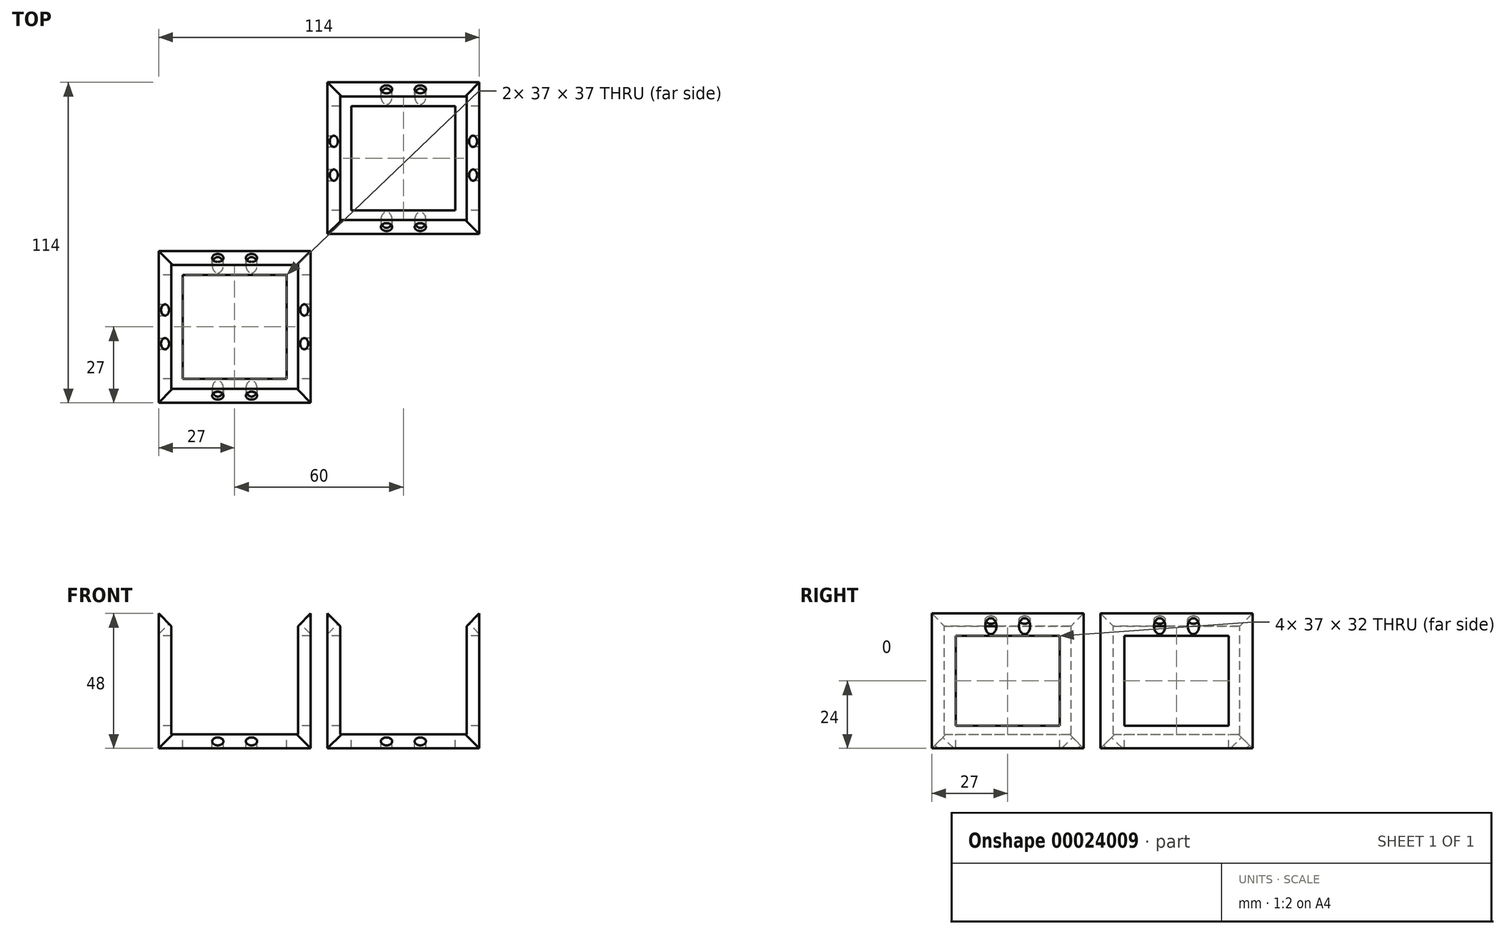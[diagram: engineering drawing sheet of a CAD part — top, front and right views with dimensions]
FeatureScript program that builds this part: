
annotation { "Feature Type Name" : "Feature", "Feature Type Description" : "" }
export const myFeature = defineFeature(function(context is Context, id is Id, definition is map)
    precondition{}
    {
        {
            var Q0;
            Q0=qCreatedBy(makeId("Top.planeOp"),FACE);
            var sketch = newSketch(context, id + "F0", { "sketchPlane" : qUnion([Q0])});
            skPoint(sketch, "E0.rect.middle", {"position": v(0, 0) * mm});
            skLineSegment(sketch, "E1.rect.bottom", {"start": v(27, 27) * mm, "end": v(-27, 27) * mm});
            skLineSegment(sketch, "E2", {"start": v(27, 27) * mm, "end": v(27, -27) * mm});
            skLineSegment(sketch, "E3", {"start": v(-27, -27) * mm, "end": v(0, -27) * mm});
            skLineSegment(sketch, "E4", {"start": v(0, -27) * mm, "end": v(27, -27) * mm});
            skLineSegment(sketch, "E5", {"start": v(-27, 27) * mm, "end": v(-27, 0) * mm});
            skLineSegment(sketch, "E6", {"start": v(-27, 0) * mm, "end": v(-27, -27) * mm});
            skSolve(sketch);
        }
        {
            var Q0;
            Q0 = qSketchRegion(id + "F0", true);
            extrude(context, id + "F1", {"entities" : qUnion([Q0]), "depth" : 48 * mm});
        }
        {
            var Q0;
            Q0=makeQuery(id+"F1.opExtrude","SWEPT_FACE",FACE,{"disambiguationData":[OSD([sQuery(id+"F0.wireOp",EDGE,"E3"),sQuery(id+"F0.wireOp",EDGE,"E4")])]});
            var sketch = newSketch(context, id + "F2", { "sketchPlane" : qUnion([Q0])});
            skLineSegment(sketch, "E7", {"start": v(-21, 48) * mm, "end": v(-21, 42) * mm});
            skLineSegment(sketch, "E8", {"start": v(-21, 42) * mm, "end": v(-27, 42) * mm});
            skLineSegment(sketch, "E9", {"start": v(-27, 48) * mm, "end": v(-21, 42) * mm});
            skLineSegment(sketch, "E10", {"start": v(-27, 6) * mm, "end": v(-21, 6) * mm});
            skLineSegment(sketch, "E11", {"start": v(-21, 6) * mm, "end": v(-21, 0) * mm});
            skLineSegment(sketch, "E12", {"start": v(-21, 42) * mm, "end": v(-21, 6) * mm});
            skLineSegment(sketch, "E13", {"start": v(0, 6) * mm, "end": v(-21, 6) * mm});
            skLineSegment(sketch, "E14", {"start": v(-27, 48) * mm, "end": v(0, 48) * mm});
            skLineSegment(sketch, "E15", {"start": v(0, 48) * mm, "end": v(0, 25.24) * mm});
            skLineSegment(sketch, "E16.MirrorCS", {"start": v(27, 48) * mm, "end": v(0, 48) * mm});
            skLineSegment(sketch, "E17.MirrorCS", {"start": v(27, 48) * mm, "end": v(21, 42) * mm});
            skLineSegment(sketch, "E18.MirrorCS", {"start": v(21, 42) * mm, "end": v(21, 6) * mm});
            skLineSegment(sketch, "E19.MirrorCS", {"start": v(0, 6) * mm, "end": v(21, 6) * mm});
            skSolve(sketch);
        }
        {
            var Q0;
            Q0 = qSketchRegion(id + "F2", true);
            extrude(context, id + "F3", {"entities" : qUnion([Q0]), "operationType" : NewBodyOperationType.REMOVE, "endBound" : BoundingType.THROUGH_ALL, "oppositeDirection" : true, "depth" : 25 * mm});
        }
        {
            var Q0;
            Q0=qCreatedBy(makeId("Right.planeOp"),FACE);
            var sketch = newSketch(context, id + "F4", { "sketchPlane" : qUnion([Q0])});
            skPoint(sketch, "E20.0", {"position": v(-27, 0) * mm});
            skLineSegment(sketch, "E21", {"start": v(-27, 0) * mm, "end": v(-21, 6) * mm});
            skPoint(sketch, "E22.0", {"position": v(-27, 6) * mm});
            skLineSegment(sketch, "E23", {"start": v(-21, 6) * mm, "end": v(-27, 6) * mm});
            skLineSegment(sketch, "E24", {"start": v(-27, 0) * mm, "end": v(-27, 6) * mm});
            skSolve(sketch);
        }
        {
            var Q0;
            Q0 = qSketchRegion(id + "F4", true);
            extrude(context, id + "F5", {"entities" : qUnion([Q0]), "operationType" : NewBodyOperationType.REMOVE, "oppositeDirection" : true, "depth" : 21 * mm, "hasSecondDirection" : true, "secondDirectionOppositeDirection" : false, "secondDirectionDepth" : 21 * mm});
        }
        {
            var Q0;
            Q0=makeQuery(id+"F5.boolean.opBoolean","COPY",FACE,{"derivedFrom":makeQuery(id+"F5.opExtrude","SWEPT_FACE",FACE,{"disambiguationData":[OSD([sQuery(id+"F4.wireOp",EDGE,"E21")])]})});
            var sketch = newSketch(context, id + "F6", { "sketchPlane" : qUnion([Q0])});
            skLineSegment(sketch, "E25", {"start": v(-21, -10.6) * mm, "end": v(-21, -19.1) * mm});
            skLineSegment(sketch, "E26", {"start": v(-21, -19.1) * mm, "end": v(-27, -19.1) * mm});
            skLineSegment(sketch, "E27", {"start": v(-21, -10.6) * mm, "end": v(-27, -19.1) * mm});
            skSolve(sketch);
        }
        {
            var Q0;
            Q0 = qSketchRegion(id + "F6", true);
            extrude(context, id + "F7", {"entities" : qUnion([Q0]), "operationType" : NewBodyOperationType.REMOVE, "endBound" : BoundingType.THROUGH_ALL, "depth" : 25 * mm});
        }
        {
            var Q0;
            Q0=makeQuery(id+"F7.boolean.opBoolean","MERGE",FACE,{"derivedFrom":[makeQuery(id+"F5.boolean.opBoolean","COPY",FACE,{"derivedFrom":makeQuery(id+"F5.opExtrude","SWEPT_FACE",FACE,{"disambiguationData":[OSD([sQuery(id+"F4.wireOp",EDGE,"E21")])]})}),makeQuery(id+"F7.opExtrude","CAP_FACE",FACE,{"disambiguationData":[OSD([sQuery(id+"F6.wireOp",EDGE,"E25"),sQuery(id+"F6.wireOp",EDGE,"E26"),sQuery(id+"F6.wireOp",EDGE,"E27")])],"isStart":true})]});
            var sketch = newSketch(context, id + "F8", { "sketchPlane" : qUnion([Q0])});
            skLineSegment(sketch, "E28", {"start": v(21, -19.1) * mm, "end": v(27, -19.1) * mm});
            skLineSegment(sketch, "E29", {"start": v(27, -19.1) * mm, "end": v(21, -10.6) * mm});
            skLineSegment(sketch, "E30", {"start": v(21, -10.6) * mm, "end": v(21, -19.1) * mm});
            skSolve(sketch);
        }
        {
            var Q0;
            Q0 = qSketchRegion(id + "F8", true);
            extrude(context, id + "F9", {"entities" : qUnion([Q0]), "operationType" : NewBodyOperationType.REMOVE, "endBound" : BoundingType.THROUGH_ALL, "depth" : 25 * mm});
        }
        {
            var Q0;
            Q0=makeQuery(id+"F3.boolean.opBoolean","COPY",FACE,{"derivedFrom":makeQuery(id+"F3.opExtrude","SWEPT_FACE",FACE,{"disambiguationData":[OSD([sQuery(id+"F2.wireOp",EDGE,"E13"),sQuery(id+"F2.wireOp",EDGE,"E19.MirrorCS")])]})});
            var sketch = newSketch(context, id + "F10", { "sketchPlane" : qUnion([Q0])});
            skLineSegment(sketch, "E31", {"start": v(-21, -21) * mm, "end": v(-21, -27) * mm});
            skLineSegment(sketch, "E32", {"start": v(-21, -27) * mm, "end": v(-27, -27) * mm});
            skLineSegment(sketch, "E33", {"start": v(-27, -27) * mm, "end": v(-21, -21) * mm});
            skSolve(sketch);
        }
        {
            var Q0;
            Q0 = qSketchRegion(id + "F10", true);
            extrude(context, id + "F11", {"entities" : qUnion([Q0]), "operationType" : NewBodyOperationType.REMOVE, "endBound" : BoundingType.THROUGH_ALL, "depth" : 25 * mm});
        }
        {
            var Q0;
            Q0=makeQuery(id+"F11.boolean.opBoolean","COPY",FACE,{"derivedFrom":makeQuery(id+"F11.opExtrude","SWEPT_FACE",FACE,{"disambiguationData":[OSD([sQuery(id+"F10.wireOp",EDGE,"E33")])]})});
            var sketch = newSketch(context, id + "F12", { "sketchPlane" : qUnion([Q0])});
            skLineSegment(sketch, "E34", {"start": v(-38.18, 6) * mm, "end": v(-38.18, 0) * mm});
            skLineSegment(sketch, "E35", {"start": v(-38.18, 0) * mm, "end": v(-29.7, 6) * mm});
            skLineSegment(sketch, "E36", {"start": v(-29.7, 6) * mm, "end": v(-38.18, 6) * mm});
            skSolve(sketch);
        }
        {
            var Q0;
            Q0 = qSketchRegion(id + "F12", true);
            extrude(context, id + "F13", {"entities" : qUnion([Q0]), "operationType" : NewBodyOperationType.REMOVE, "endBound" : BoundingType.THROUGH_ALL, "depth" : 25 * mm});
        }
        {
            var Q0;
            Q0=makeQuery(id+"F3.boolean.opBoolean","COPY",FACE,{"derivedFrom":makeQuery(id+"F3.opExtrude","SWEPT_FACE",FACE,{"disambiguationData":[OSD([sQuery(id+"F2.wireOp",EDGE,"E13"),sQuery(id+"F2.wireOp",EDGE,"E19.MirrorCS")])]})});
            var sketch = newSketch(context, id + "F14", { "sketchPlane" : qUnion([Q0])});
            skLineSegment(sketch, "E37", {"start": v(21, -21) * mm, "end": v(21, -27) * mm});
            skLineSegment(sketch, "E38", {"start": v(21, -27) * mm, "end": v(27, -27) * mm});
            skLineSegment(sketch, "E39", {"start": v(21, -21) * mm, "end": v(27, -27) * mm});
            skSolve(sketch);
        }
        {
            var Q0;
            Q0 = qSketchRegion(id + "F14", true);
            extrude(context, id + "F15", {"entities" : qUnion([Q0]), "operationType" : NewBodyOperationType.REMOVE, "endBound" : BoundingType.THROUGH_ALL, "depth" : 25 * mm});
        }
        {
            var Q0;
            Q0=makeQuery(id+"F15.boolean.opBoolean","COPY",FACE,{"derivedFrom":makeQuery(id+"F15.opExtrude","SWEPT_FACE",FACE,{"disambiguationData":[OSD([sQuery(id+"F14.wireOp",EDGE,"E39")])]})});
            var sketch = newSketch(context, id + "F16", { "sketchPlane" : qUnion([Q0])});
            skLineSegment(sketch, "E40", {"start": v(29.7, 6) * mm, "end": v(38.18, 6) * mm});
            skLineSegment(sketch, "E41", {"start": v(38.18, 6) * mm, "end": v(38.18, 0) * mm});
            skLineSegment(sketch, "E42", {"start": v(38.18, 0) * mm, "end": v(29.7, 6) * mm});
            skSolve(sketch);
        }
        {
            var Q0;
            Q0 = qSketchRegion(id + "F16", true);
            extrude(context, id + "F17", {"entities" : qUnion([Q0]), "operationType" : NewBodyOperationType.REMOVE, "endBound" : BoundingType.THROUGH_ALL, "depth" : 25 * mm});
        }
        {
            var Q0;
            Q0=qCreatedBy(makeId("Right.planeOp"),FACE);
            var sketch = newSketch(context, id + "F18", { "sketchPlane" : qUnion([Q0])});
            skPoint(sketch, "E43.0", {"position": v(27, 6) * mm});
            skPoint(sketch, "E44.0", {"position": v(27, 0) * mm});
            skLineSegment(sketch, "E45", {"start": v(27, 6) * mm, "end": v(21, 6) * mm});
            skLineSegment(sketch, "E46", {"start": v(21, 6) * mm, "end": v(27, 0) * mm});
            skLineSegment(sketch, "E47", {"start": v(27, 6) * mm, "end": v(27, 0) * mm});
            skSolve(sketch);
        }
        {
            var Q0;
            Q0 = qSketchRegion(id + "F18", true);
            extrude(context, id + "F19", {"entities" : qUnion([Q0]), "operationType" : NewBodyOperationType.REMOVE, "oppositeDirection" : true, "depth" : 21 * mm, "hasSecondDirection" : true, "secondDirectionOppositeDirection" : false, "secondDirectionDepth" : 21 * mm});
        }
        {
            var Q0;
            Q0=makeQuery(id+"F19.boolean.opBoolean","COPY",FACE,{"derivedFrom":makeQuery(id+"F19.opExtrude","SWEPT_FACE",FACE,{"disambiguationData":[OSD([sQuery(id+"F18.wireOp",EDGE,"E46")])]})});
            var sketch = newSketch(context, id + "F20", { "sketchPlane" : qUnion([Q0])});
            skPoint(sketch, "E48.0", {"position": v(-27, -19.1) * mm});
            skLineSegment(sketch, "E49", {"start": v(-21, -10.6) * mm, "end": v(-27, -19.1) * mm});
            skLineSegment(sketch, "E50", {"start": v(-21, -19.1) * mm, "end": v(-21, -10.6) * mm});
            skLineSegment(sketch, "E51", {"start": v(-21, -19.1) * mm, "end": v(-27, -19.1) * mm});
            skSolve(sketch);
        }
        {
            var Q0;
            Q0 = qSketchRegion(id + "F20", true);
            extrude(context, id + "F21", {"entities" : qUnion([Q0]), "operationType" : NewBodyOperationType.REMOVE, "endBound" : BoundingType.THROUGH_ALL, "depth" : 25 * mm});
        }
        {
            var Q0;
            Q0=makeQuery(id+"F21.boolean.opBoolean","MERGE",FACE,{"derivedFrom":[makeQuery(id+"F19.boolean.opBoolean","COPY",FACE,{"derivedFrom":makeQuery(id+"F19.opExtrude","SWEPT_FACE",FACE,{"disambiguationData":[OSD([sQuery(id+"F18.wireOp",EDGE,"E46")])]})}),makeQuery(id+"F21.opExtrude","CAP_FACE",FACE,{"disambiguationData":[OSD([sQuery(id+"F20.wireOp",EDGE,"E49"),sQuery(id+"F20.wireOp",EDGE,"E50"),sQuery(id+"F20.wireOp",EDGE,"E51")])],"isStart":true})]});
            var sketch = newSketch(context, id + "F22", { "sketchPlane" : qUnion([Q0])});
            skLineSegment(sketch, "E52", {"start": v(21, -10.6) * mm, "end": v(21, -19.1) * mm});
            skPoint(sketch, "E53.0", {"position": v(27, -19.1) * mm});
            skLineSegment(sketch, "E54", {"start": v(27, -19.1) * mm, "end": v(21, -19.1) * mm});
            skLineSegment(sketch, "E55", {"start": v(27, -19.1) * mm, "end": v(21, -10.6) * mm});
            skSolve(sketch);
        }
        {
            var Q0;
            Q0 = qSketchRegion(id + "F22", true);
            extrude(context, id + "F23", {"entities" : qUnion([Q0]), "operationType" : NewBodyOperationType.REMOVE, "endBound" : BoundingType.THROUGH_ALL, "depth" : 25 * mm});
        }
        {
            var Q0;
            Q0=makeQuery(id+"F3.boolean.opBoolean","COPY",FACE,{"derivedFrom":makeQuery(id+"F3.opExtrude","SWEPT_FACE",FACE,{"disambiguationData":[OSD([sQuery(id+"F2.wireOp",EDGE,"E13"),sQuery(id+"F2.wireOp",EDGE,"E19.MirrorCS")])]})});
            var sketch = newSketch(context, id + "F24", { "sketchPlane" : qUnion([Q0])});
            skPoint(sketch, "E56.0", {"position": v(27, 27) * mm});
            skPoint(sketch, "E57.0", {"position": v(21, 27) * mm});
            skLineSegment(sketch, "E58", {"start": v(21, 21) * mm, "end": v(21, 27) * mm});
            skLineSegment(sketch, "E59", {"start": v(27, 27) * mm, "end": v(21, 27) * mm});
            skLineSegment(sketch, "E60", {"start": v(27, 27) * mm, "end": v(21, 21) * mm});
            skSolve(sketch);
        }
        {
            var Q0;
            Q0 = qSketchRegion(id + "F24", true);
            extrude(context, id + "F25", {"entities" : qUnion([Q0]), "operationType" : NewBodyOperationType.REMOVE, "endBound" : BoundingType.THROUGH_ALL, "depth" : 25 * mm});
        }
        {
            var Q0;
            Q0=makeQuery(id+"F3.boolean.opBoolean","COPY",FACE,{"derivedFrom":makeQuery(id+"F3.opExtrude","SWEPT_FACE",FACE,{"disambiguationData":[OSD([sQuery(id+"F2.wireOp",EDGE,"E13"),sQuery(id+"F2.wireOp",EDGE,"E19.MirrorCS")])]})});
            var sketch = newSketch(context, id + "F26", { "sketchPlane" : qUnion([Q0])});
            skPoint(sketch, "E61.0", {"position": v(-27, 27) * mm});
            skPoint(sketch, "E62.0", {"position": v(-21, 27) * mm});
            skLineSegment(sketch, "E63", {"start": v(-21, 21) * mm, "end": v(-21, 27) * mm});
            skLineSegment(sketch, "E64", {"start": v(-21, 27) * mm, "end": v(-27, 27) * mm});
            skLineSegment(sketch, "E65", {"start": v(-27, 27) * mm, "end": v(-21, 21) * mm});
            skSolve(sketch);
        }
        {
            var Q0;
            Q0 = qSketchRegion(id + "F26", true);
            extrude(context, id + "F27", {"entities" : qUnion([Q0]), "operationType" : NewBodyOperationType.REMOVE, "endBound" : BoundingType.THROUGH_ALL, "depth" : 25 * mm});
        }
        {
            var Q0;
            Q0=makeQuery(id+"F25.boolean.opBoolean","COPY",FACE,{"derivedFrom":makeQuery(id+"F25.opExtrude","SWEPT_FACE",FACE,{"disambiguationData":[OSD([sQuery(id+"F24.wireOp",EDGE,"E60")])]})});
            var sketch = newSketch(context, id + "F28", { "sketchPlane" : qUnion([Q0])});
            skPoint(sketch, "E66.0", {"position": v(-29.7, 6) * mm});
            skPoint(sketch, "E67.0", {"position": v(-38.18, 6) * mm});
            skPoint(sketch, "E68.0", {"position": v(-38.18, 0) * mm});
            skLineSegment(sketch, "E69", {"start": v(-29.7, 6) * mm, "end": v(-38.18, 6) * mm});
            skLineSegment(sketch, "E70", {"start": v(-38.18, 0) * mm, "end": v(-38.18, 6) * mm});
            skLineSegment(sketch, "E71", {"start": v(-38.18, 0) * mm, "end": v(-29.7, 6) * mm});
            skSolve(sketch);
        }
        {
            var Q0;
            Q0 = qSketchRegion(id + "F28", true);
            extrude(context, id + "F29", {"entities" : qUnion([Q0]), "operationType" : NewBodyOperationType.REMOVE, "endBound" : BoundingType.THROUGH_ALL, "depth" : 25 * mm});
        }
        {
            var Q0;
            Q0=makeQuery(id+"F27.boolean.opBoolean","COPY",FACE,{"derivedFrom":makeQuery(id+"F27.opExtrude","SWEPT_FACE",FACE,{"disambiguationData":[OSD([sQuery(id+"F26.wireOp",EDGE,"E65")])]})});
            var sketch = newSketch(context, id + "F30", { "sketchPlane" : qUnion([Q0])});
            skPoint(sketch, "E72.0", {"position": v(38.18, 0) * mm});
            skLineSegment(sketch, "E73", {"start": v(29.7, 6) * mm, "end": v(38.18, 0) * mm});
            skLineSegment(sketch, "E74", {"start": v(38.18, 6) * mm, "end": v(38.18, 0) * mm});
            skLineSegment(sketch, "E75", {"start": v(38.18, 6) * mm, "end": v(29.7, 6) * mm});
            skSolve(sketch);
        }
        {
            var Q0;
            Q0 = qSketchRegion(id + "F30", true);
            extrude(context, id + "F31", {"entities" : qUnion([Q0]), "operationType" : NewBodyOperationType.REMOVE, "endBound" : BoundingType.THROUGH_ALL, "depth" : 25 * mm});
        }
        {
            var Q0;
            Q0=makeQuery(id+"F3.boolean.opBoolean","COPY",FACE,{"derivedFrom":makeQuery(id+"F3.opExtrude","SWEPT_FACE",FACE,{"disambiguationData":[OSD([sQuery(id+"F2.wireOp",EDGE,"E13"),sQuery(id+"F2.wireOp",EDGE,"E19.MirrorCS")])]})});
            var sketch = newSketch(context, id + "F32", { "sketchPlane" : qUnion([Q0])});
            skLineSegment(sketch, "E76.rect.bottom", {"start": v(-22.5, -22.5) * mm, "end": v(22.5, -22.5) * mm});
            skLineSegment(sketch, "E76.rect.top", {"start": v(-22.5, 22.5) * mm, "end": v(22.5, 22.5) * mm});
            skLineSegment(sketch, "E76.rect.left", {"start": v(-22.5, -22.5) * mm, "end": v(-22.5, 22.5) * mm});
            skLineSegment(sketch, "E76.rect.right", {"start": v(22.5, -22.5) * mm, "end": v(22.5, 22.5) * mm});
            skPoint(sketch, "E76.rect.middle", {"position": v(0, 0) * mm});
            skSolve(sketch);
        }
        {
            var Q0;
            Q0 = qSketchRegion(id + "F32", true);
            extrude(context, id + "F33", {"entities" : qUnion([Q0]), "operationType" : NewBodyOperationType.REMOVE, "oppositeDirection" : true, "depth" : 1 * mm, "hasSecondDirection" : true, "secondDirectionBound" : SecondDirectionBoundingType.THROUGH_ALL, "secondDirectionOppositeDirection" : false, "secondDirectionDepth" : 25 * mm});
        }
        {
            var Q0;
            Q0=makeQuery(id+"F33.boolean.opBoolean","COPY",FACE,{"derivedFrom":makeQuery(id+"F33.opExtrude","CAP_FACE",FACE,{"disambiguationData":[OSD([sQuery(id+"F32.wireOp",EDGE,"E76.rect.bottom"),sQuery(id+"F32.wireOp",EDGE,"E76.rect.top"),sQuery(id+"F32.wireOp",EDGE,"E76.rect.left"),sQuery(id+"F32.wireOp",EDGE,"E76.rect.right")])],"isStart":false})});
            var sketch = newSketch(context, id + "F34", { "sketchPlane" : qUnion([Q0])});
            skLineSegment(sketch, "E77.rect.bottom", {"start": v(-18.5, -18.5) * mm, "end": v(18.5, -18.5) * mm});
            skLineSegment(sketch, "E77.rect.top", {"start": v(-18.5, 18.5) * mm, "end": v(18.5, 18.5) * mm});
            skLineSegment(sketch, "E77.rect.left", {"start": v(-18.5, -18.5) * mm, "end": v(-18.5, 18.5) * mm});
            skLineSegment(sketch, "E77.rect.right", {"start": v(18.5, -18.5) * mm, "end": v(18.5, 18.5) * mm});
            skPoint(sketch, "E77.rect.middle", {"position": v(0, 0) * mm});
            skSolve(sketch);
        }
        {
            var Q0;
            Q0 = qSketchRegion(id + "F34", true);
            extrude(context, id + "F35", {"entities" : qUnion([Q0]), "operationType" : NewBodyOperationType.REMOVE, "endBound" : BoundingType.THROUGH_ALL, "oppositeDirection" : true, "depth" : 25 * mm});
        }
        {
            var Q0;
            Q0=makeQuery(id+"F1.opExtrude","SWEPT_FACE",FACE,{"disambiguationData":[OSD([sQuery(id+"F0.wireOp",EDGE,"E5"),sQuery(id+"F0.wireOp",EDGE,"E6")])]});
            var sketch = newSketch(context, id + "F36", { "sketchPlane" : qUnion([Q0])});
            skLineSegment(sketch, "E78", {"start": v(0, 0) * mm, "end": v(0, 48) * mm});
            skLineSegment(sketch, "E79.rect.bottom", {"start": v(18.5, 8) * mm, "end": v(-18.5, 8) * mm});
            skLineSegment(sketch, "E79.rect.top", {"start": v(18.5, 40) * mm, "end": v(-18.5, 40) * mm});
            skLineSegment(sketch, "E79.rect.left", {"start": v(18.5, 8) * mm, "end": v(18.5, 40) * mm});
            skLineSegment(sketch, "E79.rect.right", {"start": v(-18.5, 8) * mm, "end": v(-18.5, 40) * mm});
            skPoint(sketch, "E79.rect.middle", {"position": v(0, 24) * mm});
            skSolve(sketch);
        }
        {
            var Q0;
            Q0 = qSketchRegion(id + "F36", true);
            extrude(context, id + "F37", {"entities" : qUnion([Q0]), "operationType" : NewBodyOperationType.REMOVE, "endBound" : BoundingType.THROUGH_ALL, "oppositeDirection" : true, "depth" : 25 * mm});
        }
        {
            var Q0;
            Q0=makeQuery(id+"F9.boolean.opBoolean","MERGE",FACE,{"derivedFrom":[makeQuery(id+"F7.boolean.opBoolean","MERGE",FACE,{"derivedFrom":[makeQuery(id+"F5.boolean.opBoolean","COPY",FACE,{"derivedFrom":makeQuery(id+"F5.opExtrude","SWEPT_FACE",FACE,{"disambiguationData":[OSD([sQuery(id+"F4.wireOp",EDGE,"E21")])]})}),makeQuery(id+"F7.opExtrude","CAP_FACE",FACE,{"disambiguationData":[OSD([sQuery(id+"F6.wireOp",EDGE,"E25"),sQuery(id+"F6.wireOp",EDGE,"E26"),sQuery(id+"F6.wireOp",EDGE,"E27")])],"isStart":true})]}),makeQuery(id+"F9.opExtrude","CAP_FACE",FACE,{"disambiguationData":[OSD([sQuery(id+"F8.wireOp",EDGE,"E28"),sQuery(id+"F8.wireOp",EDGE,"E29"),sQuery(id+"F8.wireOp",EDGE,"E30")])],"isStart":true})]});
            var sketch = newSketch(context, id + "F38", { "sketchPlane" : qUnion([Q0])});
            skLineSegment(sketch, "E80", {"start": v(0, -12.02) * mm, "end": v(0, -19.1) * mm});
            skLineSegment(sketch, "E81", {"start": v(0, -15.56) * mm, "end": v(6, -15.56) * mm});
            skCircle(sketch, "E82", {"center": v(6, -15.56) * mm, "radius": 2 * mm});
            skCircle(sketch, "E83.MirrorC", {"center": v(-6, -15.56) * mm, "radius": 2 * mm});
            skSolve(sketch);
        }
        {
            var Q0;
            Q0 = qSketchRegion(id + "F38", true);
            extrude(context, id + "F39", {"entities" : qUnion([Q0]), "operationType" : NewBodyOperationType.REMOVE, "endBound" : BoundingType.THROUGH_ALL, "oppositeDirection" : true, "depth" : 25 * mm});
        }
        {
            var Q0;
            Q0=makeQuery(id+"F23.boolean.opBoolean","MERGE",FACE,{"derivedFrom":[makeQuery(id+"F21.boolean.opBoolean","MERGE",FACE,{"derivedFrom":[makeQuery(id+"F19.boolean.opBoolean","COPY",FACE,{"derivedFrom":makeQuery(id+"F19.opExtrude","SWEPT_FACE",FACE,{"disambiguationData":[OSD([sQuery(id+"F18.wireOp",EDGE,"E46")])]})}),makeQuery(id+"F21.opExtrude","CAP_FACE",FACE,{"disambiguationData":[OSD([sQuery(id+"F20.wireOp",EDGE,"E49"),sQuery(id+"F20.wireOp",EDGE,"E50"),sQuery(id+"F20.wireOp",EDGE,"E51")])],"isStart":true})]}),makeQuery(id+"F23.opExtrude","CAP_FACE",FACE,{"disambiguationData":[OSD([sQuery(id+"F22.wireOp",EDGE,"E52"),sQuery(id+"F22.wireOp",EDGE,"E54"),sQuery(id+"F22.wireOp",EDGE,"E55")])],"isStart":true})]});
            var sketch = newSketch(context, id + "F40", { "sketchPlane" : qUnion([Q0])});
            skLineSegment(sketch, "E84", {"start": v(0, -19.1) * mm, "end": v(0, -12.02) * mm});
            skLineSegment(sketch, "E85", {"start": v(0, -15.56) * mm, "end": v(6, -15.56) * mm});
            skCircle(sketch, "E86", {"center": v(6, -15.56) * mm, "radius": 2 * mm});
            skCircle(sketch, "E87.MirrorC", {"center": v(-6, -15.56) * mm, "radius": 2 * mm});
            skSolve(sketch);
        }
        {
            var Q0;
            Q0 = qSketchRegion(id + "F40", true);
            extrude(context, id + "F41", {"entities" : qUnion([Q0]), "operationType" : NewBodyOperationType.REMOVE, "endBound" : BoundingType.THROUGH_ALL, "oppositeDirection" : true, "depth" : 25 * mm});
        }
        {
            var Q0;
            Q0=makeQuery(id+"F3.boolean.opBoolean","COPY",FACE,{"derivedFrom":makeQuery(id+"F3.opExtrude","SWEPT_FACE",FACE,{"disambiguationData":[OSD([sQuery(id+"F2.wireOp",EDGE,"E17.MirrorCS")])]})});
            var sketch = newSketch(context, id + "F42", { "sketchPlane" : qUnion([Q0])});
            skLineSegment(sketch, "E88", {"start": v(0, 46.67) * mm, "end": v(0, 53.03) * mm});
            skLineSegment(sketch, "E89", {"start": v(0, 53.03) * mm, "end": v(0, 49.85) * mm});
            skLineSegment(sketch, "E90", {"start": v(0, 49.85) * mm, "end": v(6, 49.85) * mm});
            skCircle(sketch, "E91", {"center": v(6, 49.85) * mm, "radius": 2 * mm});
            skCircle(sketch, "E92.MirrorC", {"center": v(-6, 49.85) * mm, "radius": 2 * mm});
            skSolve(sketch);
        }
        {
            var Q0;
            Q0 = qSketchRegion(id + "F42", true);
            extrude(context, id + "F43", {"entities" : qUnion([Q0]), "operationType" : NewBodyOperationType.REMOVE, "endBound" : BoundingType.THROUGH_ALL, "oppositeDirection" : true, "depth" : 25 * mm});
        }
        {
            var Q0;
            Q0=makeQuery(id+"F3.boolean.opBoolean","COPY",FACE,{"derivedFrom":makeQuery(id+"F3.opExtrude","SWEPT_FACE",FACE,{"disambiguationData":[OSD([sQuery(id+"F2.wireOp",EDGE,"E9")])]})});
            var sketch = newSketch(context, id + "F44", { "sketchPlane" : qUnion([Q0])});
            skLineSegment(sketch, "E93", {"start": v(0, 53.03) * mm, "end": v(0, 46.67) * mm});
            skLineSegment(sketch, "E94", {"start": v(0, 46.67) * mm, "end": v(0, 49.85) * mm});
            skLineSegment(sketch, "E95", {"start": v(0, 49.85) * mm, "end": v(-6, 49.85) * mm});
            skCircle(sketch, "E96", {"center": v(-6, 49.85) * mm, "radius": 2 * mm});
            skCircle(sketch, "E97.MirrorC", {"center": v(6, 49.85) * mm, "radius": 2 * mm});
            skSolve(sketch);
        }
        {
            var Q0;
            Q0 = qSketchRegion(id + "F44", true);
            extrude(context, id + "F45", {"entities" : qUnion([Q0]), "operationType" : NewBodyOperationType.REMOVE, "endBound" : BoundingType.THROUGH_ALL, "oppositeDirection" : true, "depth" : 25 * mm});
        }
        {
            var Q0;
            Q0=makeQuery(id+"F1.opExtrude","SWEPT_BODY",BODY,{"disambiguationData":[OSD([sQuery(id+"F0.wireOp",EDGE,"E1.rect.bottom"),sQuery(id+"F0.wireOp",EDGE,"E2"),sQuery(id+"F0.wireOp",EDGE,"E3"),sQuery(id+"F0.wireOp",EDGE,"E4"),sQuery(id+"F0.wireOp",EDGE,"E5"),sQuery(id+"F0.wireOp",EDGE,"E6")])]});
            transform(context, id + "F46", {"entities" : qUnion([Q0]), "transformType" : TransformType.TRANSLATION_3D, "dx" : 60 * mm, "dy" : 60 * mm, "dz" : 0 * mm, "makeCopy" : true});
        }
    });
